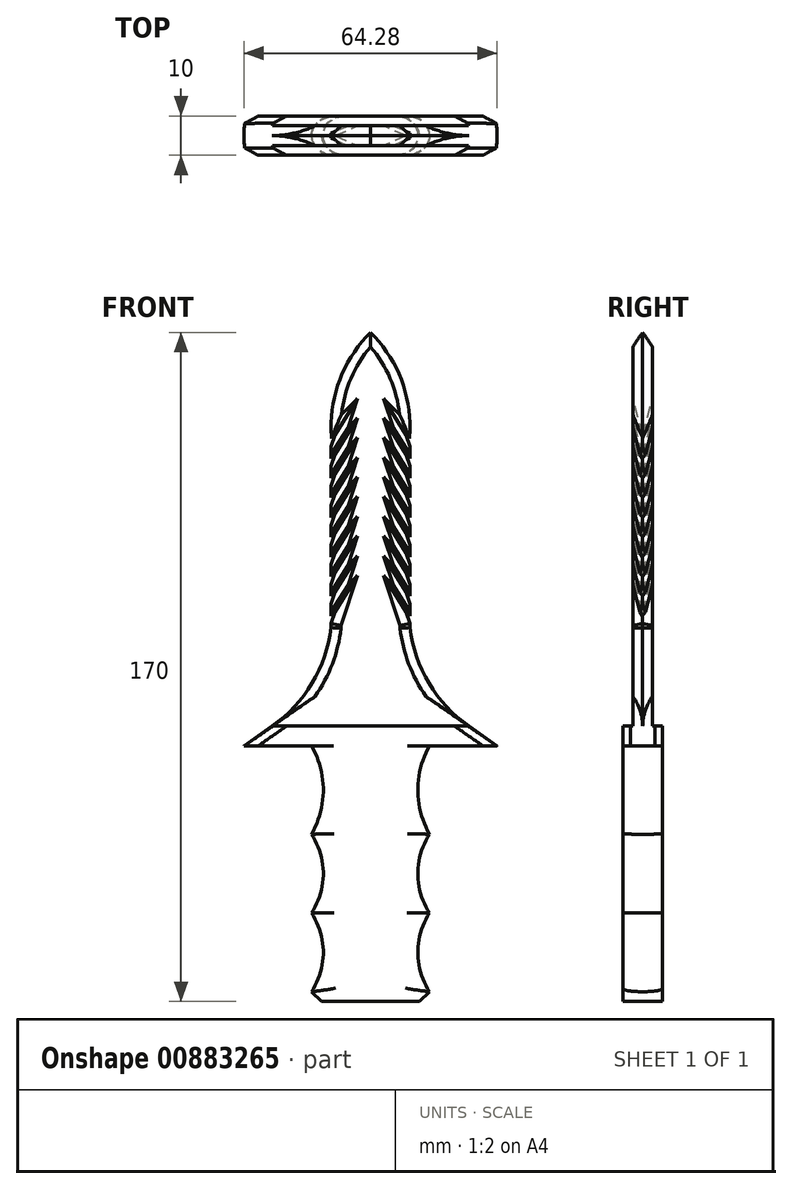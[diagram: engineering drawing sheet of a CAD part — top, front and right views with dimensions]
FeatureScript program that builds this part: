
annotation { "Feature Type Name" : "Feature", "Feature Type Description" : "" }
export const myFeature = defineFeature(function(context is Context, id is Id, definition is map)
    precondition{}
    {
        {
            var Q0;
            Q0=qCreatedBy(makeId("Front.planeOp"),FACE);
            var sketch = newSketch(context, id + "F0", { "sketchPlane" : qUnion([Q0])});
            skLineSegment(sketch, "E0", {"start": v(0, 0) * mm, "end": v(-25, 0) * mm});
            skLineSegment(sketch, "E1", {"start": v(-25, 0) * mm, "end": v(-32.14, -5) * mm});
            skLineSegment(sketch, "E2", {"start": v(-32.14, -5) * mm, "end": v(0, -5) * mm});
            skLineSegment(sketch, "E3", {"start": v(0, 0) * mm, "end": v(0, -5) * mm});
            skLineSegment(sketch, "E4", {"start": v(0, 15.57) * mm, "end": v(0, -20.87) * mm, "construction": true});
            skLineSegment(sketch, "E5", {"start": v(0, -5) * mm, "end": v(0, -70) * mm});
            skLineSegment(sketch, "E6", {"start": v(0, -70) * mm, "end": v(-15, -70) * mm});
            skLineSegment(sketch, "E7", {"start": v(-15, -70) * mm, "end": v(-15, -5) * mm});
            skLineSegment(sketch, "E8", {"start": v(-15, -67.5) * mm, "end": v(-12.5, -70) * mm});
            skLineSegment(sketch, "E9", {"start": v(-10, 25) * mm, "end": v(-10, 77.06) * mm});
            skArc(sketch, "E10", {"start": v(-25, 0) * mm, "mid": v(-14.84, 10.9) * mm, "end": v(-10, 25) * mm});
            skArc(sketch, "E11", {"start": v(0, 100) * mm, "mid": v(-7.6, 88.54) * mm, "end": v(-10, 75) * mm});
            skLineSegment(sketch, "E12", {"start": v(0, 100) * mm, "end": v(0, 0) * mm});
            skArc(sketch, "E13", {"start": v(-15, -67.5) * mm, "mid": v(-12, -57.5) * mm, "end": v(-15, -47.5) * mm});
            skArc(sketch, "E14", {"start": v(-15, -47.5) * mm, "mid": v(-12, -37.5) * mm, "end": v(-15, -27.5) * mm});
            skArc(sketch, "E15", {"start": v(-15, -27.5) * mm, "mid": v(-12, -16.25) * mm, "end": v(-15, -5) * mm});
            skLineSegment(sketch, "E16", {"start": v(-10, 73) * mm, "end": v(-9, 74) * mm});
            skLineSegment(sketch, "E17", {"start": v(-9, 74) * mm, "end": v(-10, 71) * mm});
            skLineSegment(sketch, "E18.1.0.0", {"start": v(-10, 68) * mm, "end": v(-9, 69) * mm});
            skLineSegment(sketch, "E18.1.0.1", {"start": v(-9, 69) * mm, "end": v(-10, 66) * mm});
            skLineSegment(sketch, "E18.2.0.0", {"start": v(-10, 63) * mm, "end": v(-9, 64) * mm});
            skLineSegment(sketch, "E18.2.0.1", {"start": v(-9, 64) * mm, "end": v(-10, 61) * mm});
            skLineSegment(sketch, "E18.3.0.0", {"start": v(-10, 58) * mm, "end": v(-9, 59) * mm});
            skLineSegment(sketch, "E18.3.0.1", {"start": v(-9, 59) * mm, "end": v(-10, 56) * mm});
            skLineSegment(sketch, "E18.4.0.0", {"start": v(-10, 53) * mm, "end": v(-9, 54) * mm});
            skLineSegment(sketch, "E18.4.0.1", {"start": v(-9, 54) * mm, "end": v(-10, 51) * mm});
            skLineSegment(sketch, "E18.5.0.0", {"start": v(-10, 48) * mm, "end": v(-9, 49) * mm});
            skLineSegment(sketch, "E18.5.0.1", {"start": v(-9, 49) * mm, "end": v(-10, 46) * mm});
            skLineSegment(sketch, "E18.6.0.0", {"start": v(-10, 43) * mm, "end": v(-9, 44) * mm});
            skLineSegment(sketch, "E18.6.0.1", {"start": v(-9, 44) * mm, "end": v(-10, 41) * mm});
            skLineSegment(sketch, "E18.7.0.0", {"start": v(-10, 38) * mm, "end": v(-9, 39) * mm});
            skLineSegment(sketch, "E18.7.0.1", {"start": v(-9, 39) * mm, "end": v(-10, 36) * mm});
            skLineSegment(sketch, "E18.8.0.0", {"start": v(-10, 33) * mm, "end": v(-9, 34) * mm});
            skLineSegment(sketch, "E18.8.0.1", {"start": v(-9, 34) * mm, "end": v(-10, 31) * mm});
            skLineSegment(sketch, "E18.9.0.0", {"start": v(-10, 28) * mm, "end": v(-9, 29) * mm});
            skLineSegment(sketch, "E18.9.0.1", {"start": v(-9, 29) * mm, "end": v(-10, 26) * mm});
            skLineSegment(sketch, "E18.direction1", {"start": v(-10, 73) * mm, "end": v(-10, 68) * mm, "construction": true});
            skSolve(sketch);
        }
        {
            var Q0;
            Q0=makeQuery(id+"F0.imprint","IMPRINT",FACE,{"disambiguationData":[TD([[makeQuery(id+"F0.imprint","IMPRINT",EDGE,{"derivedFrom":sQuery(id+"F0.wireOp",EDGE,"E0")}),1.0]])]});
            var Q1;
            {var subQ5=sQuery(id+"F0.wireOp",EDGE,"E5");Q1=makeQuery(id+"F0.imprint","IMPRINT",FACE,{"disambiguationData":[TD([[makeQuery(id+"F0.imprint","IMPRINT",EDGE,{"derivedFrom":subQ5}),-1.0]])]});}
            var Q2;
            Q2=sQuery(id+"F0.wireOp",EDGE,"E4");
            revolve(context, id + "F1", {"surfaceOperationType" : NewSurfaceOperationType.NEW, "entities" : qUnion([Q0, Q1]), "axis" : qUnion([Q2]), "revolveType" : RevolveType.FULL});
        }
        {
            var Q0;
            Q0=makeQuery(id+"F0.imprint","IMPRINT",FACE,{"disambiguationData":[TD([[makeQuery(id+"F0.imprint","IMPRINT",EDGE,{"derivedFrom":sQuery(id+"F0.wireOp",EDGE,"E0")}),-1.0]])]});
            extrude(context, id + "F2", {"entities" : qUnion([Q0]), "operationType" : NewBodyOperationType.ADD, "depth" : 2.5 * mm, "offsetDistance" : 25 * mm});
        }
        {
            var Q0;
            Q0=makeQuery(id+"F2.opExtrude","CAP_EDGE",EDGE,{"disambiguationData":[OSD([sQuery(id+"F0.wireOp",EDGE,"E10")])],"isStart":false});
            var Q1;
            {var subQ0=sQuery(id+"F0.wireOp",EDGE,"E9");Q1=makeQuery(id+"F2.opExtrude","CAP_EDGE",EDGE,{"disambiguationData":[OSD([subQ0]),TDD([makeQuery(id+"F0.imprint","IMPRINT",EDGE,{"disambiguationData":[TD([[makeQuery(id+"F0.imprint","INTERSECT",VERTEX,{"derivedFrom":[subQ0,sQuery(id+"F0.wireOp",EDGE,"E10")]}),-1.0]])],"derivedFrom":subQ0})])],"isStart":false});}
            var Q2;
            Q2=makeQuery(id+"F2.opExtrude","CAP_EDGE",EDGE,{"disambiguationData":[OSD([sQuery(id+"F0.wireOp",EDGE,"E18.9.0.1")])],"isStart":false});
            var Q3;
            Q3=makeQuery(id+"F2.opExtrude","CAP_EDGE",EDGE,{"disambiguationData":[OSD([sQuery(id+"F0.wireOp",EDGE,"E18.9.0.0")])],"isStart":false});
            var Q4;
            {var subQ0=sQuery(id+"F0.wireOp",EDGE,"E9");Q4=makeQuery(id+"F2.opExtrude","CAP_EDGE",EDGE,{"disambiguationData":[OSD([subQ0]),TDD([makeQuery(id+"F0.imprint","IMPRINT",EDGE,{"disambiguationData":[TD([[makeQuery(id+"F0.imprint","INTERSECT",VERTEX,{"derivedFrom":[subQ0,sQuery(id+"F0.wireOp",EDGE,"E18.8.0.1")]}),1.0]])],"derivedFrom":subQ0})])],"isStart":false});}
            var Q5;
            Q5=makeQuery(id+"F2.opExtrude","CAP_EDGE",EDGE,{"disambiguationData":[OSD([sQuery(id+"F0.wireOp",EDGE,"E18.8.0.1")])],"isStart":false});
            var Q6;
            Q6=makeQuery(id+"F2.opExtrude","CAP_EDGE",EDGE,{"disambiguationData":[OSD([sQuery(id+"F0.wireOp",EDGE,"E18.8.0.0")])],"isStart":false});
            var Q7;
            {var subQ0=sQuery(id+"F0.wireOp",EDGE,"E9");Q7=makeQuery(id+"F2.opExtrude","CAP_EDGE",EDGE,{"disambiguationData":[OSD([subQ0]),TDD([makeQuery(id+"F0.imprint","IMPRINT",EDGE,{"disambiguationData":[TD([[makeQuery(id+"F0.imprint","INTERSECT",VERTEX,{"derivedFrom":[subQ0,sQuery(id+"F0.wireOp",EDGE,"E18.7.0.1")]}),1.0]])],"derivedFrom":subQ0})])],"isStart":false});}
            var Q8;
            Q8=makeQuery(id+"F2.opExtrude","CAP_EDGE",EDGE,{"disambiguationData":[OSD([sQuery(id+"F0.wireOp",EDGE,"E18.7.0.1")])],"isStart":false});
            var Q9;
            Q9=makeQuery(id+"F2.opExtrude","CAP_EDGE",EDGE,{"disambiguationData":[OSD([sQuery(id+"F0.wireOp",EDGE,"E18.7.0.0")])],"isStart":false});
            var Q10;
            {var subQ0=sQuery(id+"F0.wireOp",EDGE,"E9");Q10=makeQuery(id+"F2.opExtrude","CAP_EDGE",EDGE,{"disambiguationData":[OSD([subQ0]),TDD([makeQuery(id+"F0.imprint","IMPRINT",EDGE,{"disambiguationData":[TD([[makeQuery(id+"F0.imprint","INTERSECT",VERTEX,{"derivedFrom":[subQ0,sQuery(id+"F0.wireOp",EDGE,"E18.6.0.1")]}),1.0]])],"derivedFrom":subQ0})])],"isStart":false});}
            var Q11;
            Q11=makeQuery(id+"F2.opExtrude","CAP_EDGE",EDGE,{"disambiguationData":[OSD([sQuery(id+"F0.wireOp",EDGE,"E18.6.0.1")])],"isStart":false});
            var Q12;
            Q12=makeQuery(id+"F2.opExtrude","CAP_EDGE",EDGE,{"disambiguationData":[OSD([sQuery(id+"F0.wireOp",EDGE,"E18.6.0.0")])],"isStart":false});
            var Q13;
            {var subQ0=sQuery(id+"F0.wireOp",EDGE,"E9");Q13=makeQuery(id+"F2.opExtrude","CAP_EDGE",EDGE,{"disambiguationData":[OSD([subQ0]),TDD([makeQuery(id+"F0.imprint","IMPRINT",EDGE,{"disambiguationData":[TD([[makeQuery(id+"F0.imprint","INTERSECT",VERTEX,{"derivedFrom":[subQ0,sQuery(id+"F0.wireOp",EDGE,"E18.5.0.1")]}),1.0]])],"derivedFrom":subQ0})])],"isStart":false});}
            var Q14;
            Q14=makeQuery(id+"F2.opExtrude","CAP_EDGE",EDGE,{"disambiguationData":[OSD([sQuery(id+"F0.wireOp",EDGE,"E18.5.0.1")])],"isStart":false});
            var Q15;
            Q15=makeQuery(id+"F2.opExtrude","CAP_EDGE",EDGE,{"disambiguationData":[OSD([sQuery(id+"F0.wireOp",EDGE,"E18.5.0.0")])],"isStart":false});
            var Q16;
            {var subQ0=sQuery(id+"F0.wireOp",EDGE,"E9");Q16=makeQuery(id+"F2.opExtrude","CAP_EDGE",EDGE,{"disambiguationData":[OSD([subQ0]),TDD([makeQuery(id+"F0.imprint","IMPRINT",EDGE,{"disambiguationData":[TD([[makeQuery(id+"F0.imprint","INTERSECT",VERTEX,{"derivedFrom":[subQ0,sQuery(id+"F0.wireOp",EDGE,"E18.4.0.1")]}),1.0]])],"derivedFrom":subQ0})])],"isStart":false});}
            var Q17;
            Q17=makeQuery(id+"F2.opExtrude","CAP_EDGE",EDGE,{"disambiguationData":[OSD([sQuery(id+"F0.wireOp",EDGE,"E18.4.0.1")])],"isStart":false});
            var Q18;
            Q18=makeQuery(id+"F2.opExtrude","CAP_EDGE",EDGE,{"disambiguationData":[OSD([sQuery(id+"F0.wireOp",EDGE,"E18.4.0.0")])],"isStart":false});
            var Q19;
            {var subQ0=sQuery(id+"F0.wireOp",EDGE,"E9");Q19=makeQuery(id+"F2.opExtrude","CAP_EDGE",EDGE,{"disambiguationData":[OSD([subQ0]),TDD([makeQuery(id+"F0.imprint","IMPRINT",EDGE,{"disambiguationData":[TD([[makeQuery(id+"F0.imprint","INTERSECT",VERTEX,{"derivedFrom":[subQ0,sQuery(id+"F0.wireOp",EDGE,"E18.3.0.1")]}),1.0]])],"derivedFrom":subQ0})])],"isStart":false});}
            var Q20;
            Q20=makeQuery(id+"F2.opExtrude","CAP_EDGE",EDGE,{"disambiguationData":[OSD([sQuery(id+"F0.wireOp",EDGE,"E18.3.0.1")])],"isStart":false});
            var Q21;
            Q21=makeQuery(id+"F2.opExtrude","CAP_EDGE",EDGE,{"disambiguationData":[OSD([sQuery(id+"F0.wireOp",EDGE,"E18.3.0.0")])],"isStart":false});
            var Q22;
            {var subQ0=sQuery(id+"F0.wireOp",EDGE,"E9");Q22=makeQuery(id+"F2.opExtrude","CAP_EDGE",EDGE,{"disambiguationData":[OSD([subQ0]),TDD([makeQuery(id+"F0.imprint","IMPRINT",EDGE,{"disambiguationData":[TD([[makeQuery(id+"F0.imprint","INTERSECT",VERTEX,{"derivedFrom":[subQ0,sQuery(id+"F0.wireOp",EDGE,"E18.2.0.1")]}),1.0]])],"derivedFrom":subQ0})])],"isStart":false});}
            var Q23;
            Q23=makeQuery(id+"F2.opExtrude","CAP_EDGE",EDGE,{"disambiguationData":[OSD([sQuery(id+"F0.wireOp",EDGE,"E18.2.0.1")])],"isStart":false});
            var Q24;
            Q24=makeQuery(id+"F2.opExtrude","CAP_EDGE",EDGE,{"disambiguationData":[OSD([sQuery(id+"F0.wireOp",EDGE,"E18.2.0.0")])],"isStart":false});
            var Q25;
            {var subQ0=sQuery(id+"F0.wireOp",EDGE,"E9");Q25=makeQuery(id+"F2.opExtrude","CAP_EDGE",EDGE,{"disambiguationData":[OSD([subQ0]),TDD([makeQuery(id+"F0.imprint","IMPRINT",EDGE,{"disambiguationData":[TD([[makeQuery(id+"F0.imprint","INTERSECT",VERTEX,{"derivedFrom":[subQ0,sQuery(id+"F0.wireOp",EDGE,"E18.1.0.1")]}),1.0]])],"derivedFrom":subQ0})])],"isStart":false});}
            var Q26;
            Q26=makeQuery(id+"F2.opExtrude","CAP_EDGE",EDGE,{"disambiguationData":[OSD([sQuery(id+"F0.wireOp",EDGE,"E18.1.0.1")])],"isStart":false});
            var Q27;
            Q27=makeQuery(id+"F2.opExtrude","CAP_EDGE",EDGE,{"disambiguationData":[OSD([sQuery(id+"F0.wireOp",EDGE,"E18.1.0.0")])],"isStart":false});
            var Q28;
            {var subQ0=sQuery(id+"F0.wireOp",EDGE,"E9");Q28=makeQuery(id+"F2.opExtrude","CAP_EDGE",EDGE,{"disambiguationData":[OSD([subQ0]),TDD([makeQuery(id+"F0.imprint","IMPRINT",EDGE,{"disambiguationData":[TD([[makeQuery(id+"F0.imprint","INTERSECT",VERTEX,{"derivedFrom":[subQ0,sQuery(id+"F0.wireOp",EDGE,"E17")]}),1.0]])],"derivedFrom":subQ0})])],"isStart":false});}
            var Q29;
            Q29=makeQuery(id+"F2.opExtrude","CAP_EDGE",EDGE,{"disambiguationData":[OSD([sQuery(id+"F0.wireOp",EDGE,"E17")])],"isStart":false});
            var Q30;
            Q30=makeQuery(id+"F2.opExtrude","CAP_EDGE",EDGE,{"disambiguationData":[OSD([sQuery(id+"F0.wireOp",EDGE,"E16")])],"isStart":false});
            var Q31;
            {var subQ0=sQuery(id+"F0.wireOp",EDGE,"E11");var subQ1=sQuery(id+"F0.wireOp",EDGE,"E9");var subQ2=makeQuery(id+"F0.imprint","INTERSECT",VERTEX,{"disambiguationData":[OD(1.0)],"derivedFrom":[subQ1,subQ0]});Q31=makeQuery(id+"F2.opExtrude","CAP_EDGE",EDGE,{"disambiguationData":[OSD([subQ1]),TDD([makeQuery(id+"F0.imprint","IMPRINT",EDGE,{"disambiguationData":[TD([[subQ2,1.0]])],"derivedFrom":subQ1}),makeQuery(id+"F0.imprint","IMPRINT",EDGE,{"disambiguationData":[TD([[makeQuery(id+"F0.imprint","INTERSECT",VERTEX,{"disambiguationData":[OD(0.0)],"derivedFrom":[subQ1,subQ0]}),1.0]])],"derivedFrom":subQ1})])],"isStart":false});}
            var Q32;
            Q32=makeQuery(id+"F2.opExtrude","CAP_EDGE",EDGE,{"disambiguationData":[OSD([sQuery(id+"F0.wireOp",EDGE,"E11")])],"isStart":false});
            chamfer(context, id + "F3", {"entities" : qUnion([Q0, Q1, Q2, Q3, Q4, Q5, Q6, Q7, Q8, Q9, Q10, Q11, Q12, Q13, Q14, Q15, Q16, Q17, Q18, Q19, Q20, Q21, Q22, Q23, Q24, Q25, Q26, Q27, Q28, Q29, Q30, Q31, Q32]), "width" : 2.5 * mm, "tangentPropagation" : true});
        }
        {
            var Q0;
            Q0=makeQuery(id+"F1.opRevolve","SWEPT_BODY",BODY,{"disambiguationData":[OSD([sQuery(id+"F0.wireOp",EDGE,"E0"),sQuery(id+"F0.wireOp",EDGE,"E1"),sQuery(id+"F0.wireOp",EDGE,"E2"),sQuery(id+"F0.wireOp",EDGE,"E3"),sQuery(id+"F0.wireOp",EDGE,"E5"),sQuery(id+"F0.wireOp",EDGE,"E6"),sQuery(id+"F0.wireOp",EDGE,"E8"),sQuery(id+"F0.wireOp",EDGE,"E13"),sQuery(id+"F0.wireOp",EDGE,"E14"),sQuery(id+"F0.wireOp",EDGE,"E15")])]});
            var Q1;
            Q1=makeQuery(id+"F0.imprint","IMPRINT",FACE,{"disambiguationData":[TD([[makeQuery(id+"F0.imprint","IMPRINT",EDGE,{"derivedFrom":sQuery(id+"F0.wireOp",EDGE,"E0")}),-1.0]])]});
            mirror(context, id + "F4", {"operationType" : NewBodyOperationType.ADD, "entities" : qUnion([Q0]), "mirrorPlane" : qUnion([Q1])});
        }
        {
            var Q0;
            Q0=makeQuery(id+"F1.opRevolve","SWEPT_BODY",BODY,{"disambiguationData":[OSD([sQuery(id+"F0.wireOp",EDGE,"E0"),sQuery(id+"F0.wireOp",EDGE,"E1"),sQuery(id+"F0.wireOp",EDGE,"E2"),sQuery(id+"F0.wireOp",EDGE,"E3"),sQuery(id+"F0.wireOp",EDGE,"E5"),sQuery(id+"F0.wireOp",EDGE,"E6"),sQuery(id+"F0.wireOp",EDGE,"E8"),sQuery(id+"F0.wireOp",EDGE,"E13"),sQuery(id+"F0.wireOp",EDGE,"E14"),sQuery(id+"F0.wireOp",EDGE,"E15")])]});
            var Q1;
            {var subQ0=makeQuery(id+"F2.opExtrude","SWEPT_FACE",FACE,{"disambiguationData":[OSD([sQuery(id+"F0.wireOp",EDGE,"E12")])]});Q1=makeQuery(id+"F4.boolean.opBoolean","MERGE",FACE,{"derivedFrom":[subQ0,makeQuery(id+"F4.opPattern","COPY",FACE,{"derivedFrom":subQ0,"instanceName":"1"})]});}
            mirror(context, id + "F5", {"operationType" : NewBodyOperationType.ADD, "entities" : qUnion([Q0]), "mirrorPlane" : qUnion([Q1])});
        }
        {
            var Q0;
            Q0=makeQuery(id+"F1.opRevolve","SWEPT_FACE",FACE,{"disambiguationData":[OSD([sQuery(id+"F0.wireOp",EDGE,"E6")])]});
            var sketch = newSketch(context, id + "F6", { "sketchPlane" : qUnion([Q0])});
            skLineSegment(sketch, "E19.bottom", {"start": v(-35, 5) * mm, "end": v(35, 5) * mm});
            skLineSegment(sketch, "E19.top", {"start": v(-35, 40) * mm, "end": v(35, 40) * mm});
            skLineSegment(sketch, "E19.left", {"start": v(-35, 5) * mm, "end": v(-35, 40) * mm});
            skLineSegment(sketch, "E19.right", {"start": v(35, 5) * mm, "end": v(35, 40) * mm});
            skPoint(sketch, "E19.middle", {"position": v(0, 22.5) * mm});
            skLineSegment(sketch, "E20.bottom", {"start": v(-35, -5) * mm, "end": v(35, -5) * mm});
            skLineSegment(sketch, "E20.top", {"start": v(-35, -40) * mm, "end": v(35, -40) * mm});
            skLineSegment(sketch, "E20.left", {"start": v(-35, -5) * mm, "end": v(-35, -40) * mm});
            skLineSegment(sketch, "E20.right", {"start": v(35, -5) * mm, "end": v(35, -40) * mm});
            skPoint(sketch, "E20.middle", {"position": v(0, -22.5) * mm});
            skSolve(sketch);
        }
        {
            var Q0;
            Q0=makeQuery(id+"F6.imprint","IMPRINT",FACE,{"disambiguationData":[TD([[makeQuery(id+"F6.imprint","IMPRINT",EDGE,{"derivedFrom":sQuery(id+"F6.wireOp",EDGE,"E19.top")}),-1.0]])]});
            var Q1;
            Q1=makeQuery(id+"F6.imprint","IMPRINT",FACE,{"disambiguationData":[TD([[makeQuery(id+"F6.imprint","IMPRINT",EDGE,{"derivedFrom":sQuery(id+"F6.wireOp",EDGE,"E20.top")}),1.0]])]});
            var Q2;
            {var subQ0=sQuery(id+"F6.wireOp",EDGE,"E20.bottom");var subQ1=makeQuery(id+"F1.opRevolve","SWEPT_EDGE",EDGE,{"disambiguationData":[OSD([sQuery(id+"F0.wireOp",EDGE,"E6"),sQuery(id+"F0.wireOp",EDGE,"E8")])]});var subQ2=makeQuery(id+"F6.imprint","INTERSECT",VERTEX,{"disambiguationData":[OD(0.0)],"derivedFrom":[subQ1,subQ0]});Q2=makeQuery(id+"F6.imprint","IMPRINT",FACE,{"disambiguationData":[TD([[makeQuery(id+"F6.imprint","IMPRINT",EDGE,{"disambiguationData":[TD([[subQ2,-1.0]])],"derivedFrom":subQ0}),-1.0]])]});}
            var Q3;
            {var subQ0=sQuery(id+"F6.wireOp",EDGE,"E19.bottom");var subQ1=makeQuery(id+"F1.opRevolve","SWEPT_EDGE",EDGE,{"disambiguationData":[OSD([sQuery(id+"F0.wireOp",EDGE,"E6"),sQuery(id+"F0.wireOp",EDGE,"E8")])]});var subQ2=makeQuery(id+"F6.imprint","INTERSECT",VERTEX,{"disambiguationData":[OD(0.0)],"derivedFrom":[subQ1,subQ0]});Q3=makeQuery(id+"F6.imprint","IMPRINT",FACE,{"disambiguationData":[TD([[makeQuery(id+"F6.imprint","IMPRINT",EDGE,{"disambiguationData":[TD([[subQ2,-1.0]])],"derivedFrom":subQ0}),1.0]])]});}
            var Q4;
            {var subQ0=sQuery(id+"F0.wireOp",EDGE,"E0");var subQ1=makeQuery(id+"F2.opExtrude","CAP_FACE",FACE,{"disambiguationData":[OSD([subQ0,sQuery(id+"F0.wireOp",EDGE,"E9"),sQuery(id+"F0.wireOp",EDGE,"E10"),sQuery(id+"F0.wireOp",EDGE,"E11"),sQuery(id+"F0.wireOp",EDGE,"E12"),sQuery(id+"F0.wireOp",EDGE,"E16"),sQuery(id+"F0.wireOp",EDGE,"E17"),sQuery(id+"F0.wireOp",EDGE,"E18.1.0.0"),sQuery(id+"F0.wireOp",EDGE,"E18.1.0.1"),sQuery(id+"F0.wireOp",EDGE,"E18.2.0.0"),sQuery(id+"F0.wireOp",EDGE,"E18.2.0.1"),sQuery(id+"F0.wireOp",EDGE,"E18.3.0.0"),sQuery(id+"F0.wireOp",EDGE,"E18.3.0.1"),sQuery(id+"F0.wireOp",EDGE,"E18.4.0.0"),sQuery(id+"F0.wireOp",EDGE,"E18.4.0.1"),sQuery(id+"F0.wireOp",EDGE,"E18.5.0.0"),sQuery(id+"F0.wireOp",EDGE,"E18.5.0.1"),sQuery(id+"F0.wireOp",EDGE,"E18.6.0.0"),sQuery(id+"F0.wireOp",EDGE,"E18.6.0.1"),sQuery(id+"F0.wireOp",EDGE,"E18.7.0.0"),sQuery(id+"F0.wireOp",EDGE,"E18.7.0.1"),sQuery(id+"F0.wireOp",EDGE,"E18.8.0.0"),sQuery(id+"F0.wireOp",EDGE,"E18.8.0.1"),sQuery(id+"F0.wireOp",EDGE,"E18.9.0.0"),sQuery(id+"F0.wireOp",EDGE,"E18.9.0.1")])],"isStart":false});Q4=makeQuery(id+"F5.boolean.opBoolean","SPLIT",FACE,{"disambiguationData":[TD([subQ1])],"derivedFrom":makeQuery(id+"F1.opRevolve","SWEPT_FACE",FACE,{"disambiguationData":[OSD([subQ0])]})});}
            extrude(context, id + "F7", {"entities" : qUnion([Q0, Q1, Q2, Q3]), "operationType" : NewBodyOperationType.REMOVE, "endBound" : BoundingType.UP_TO_SURFACE, "oppositeDirection" : true, "depth" : 25 * mm, "endBoundEntityFace" : qUnion([Q4]), "offsetDistance" : 25 * mm});
        }
        {
            var Q0;
            Q0=makeQuery(id+"F7.boolean.opBoolean","INTERSECT",EDGE,{"disambiguationData":[OD(0.0)],"derivedFrom":[makeQuery(id+"F1.opRevolve","SWEPT_FACE",FACE,{"disambiguationData":[OSD([sQuery(id+"F0.wireOp",EDGE,"E15")])]}),makeQuery(id+"F7.opExtrude","SWEPT_FACE",FACE,{"disambiguationData":[OSD([sQuery(id+"F6.wireOp",EDGE,"E19.bottom")])]})]});
            var Q1;
            Q1=makeQuery(id+"F7.boolean.opBoolean","INTERSECT",EDGE,{"disambiguationData":[OD(0.0)],"derivedFrom":[makeQuery(id+"F1.opRevolve","SWEPT_FACE",FACE,{"disambiguationData":[OSD([sQuery(id+"F0.wireOp",EDGE,"E14")])]}),makeQuery(id+"F7.opExtrude","SWEPT_FACE",FACE,{"disambiguationData":[OSD([sQuery(id+"F6.wireOp",EDGE,"E19.bottom")])]})]});
            var Q2;
            Q2=makeQuery(id+"F7.boolean.opBoolean","INTERSECT",EDGE,{"disambiguationData":[OD(0.0)],"derivedFrom":[makeQuery(id+"F1.opRevolve","SWEPT_FACE",FACE,{"disambiguationData":[OSD([sQuery(id+"F0.wireOp",EDGE,"E13")])]}),makeQuery(id+"F7.opExtrude","SWEPT_FACE",FACE,{"disambiguationData":[OSD([sQuery(id+"F6.wireOp",EDGE,"E19.bottom")])]})]});
            var Q3;
            Q3=makeQuery(id+"F7.boolean.opBoolean","INTERSECT",EDGE,{"disambiguationData":[OD(0.0)],"derivedFrom":[makeQuery(id+"F1.opRevolve","SWEPT_FACE",FACE,{"disambiguationData":[OSD([sQuery(id+"F0.wireOp",EDGE,"E8")])]}),makeQuery(id+"F7.opExtrude","SWEPT_FACE",FACE,{"disambiguationData":[OSD([sQuery(id+"F6.wireOp",EDGE,"E19.bottom")])]})]});
            var Q4;
            Q4=makeQuery(id+"F7.boolean.opBoolean","INTERSECT",EDGE,{"disambiguationData":[OD(1.0)],"derivedFrom":[makeQuery(id+"F1.opRevolve","SWEPT_FACE",FACE,{"disambiguationData":[OSD([sQuery(id+"F0.wireOp",EDGE,"E8")])]}),makeQuery(id+"F7.opExtrude","SWEPT_FACE",FACE,{"disambiguationData":[OSD([sQuery(id+"F6.wireOp",EDGE,"E19.bottom")])]})]});
            var Q5;
            Q5=makeQuery(id+"F7.boolean.opBoolean","INTERSECT",EDGE,{"disambiguationData":[OD(1.0)],"derivedFrom":[makeQuery(id+"F1.opRevolve","SWEPT_FACE",FACE,{"disambiguationData":[OSD([sQuery(id+"F0.wireOp",EDGE,"E13")])]}),makeQuery(id+"F7.opExtrude","SWEPT_FACE",FACE,{"disambiguationData":[OSD([sQuery(id+"F6.wireOp",EDGE,"E19.bottom")])]})]});
            var Q6;
            Q6=makeQuery(id+"F7.boolean.opBoolean","INTERSECT",EDGE,{"disambiguationData":[OD(1.0)],"derivedFrom":[makeQuery(id+"F1.opRevolve","SWEPT_FACE",FACE,{"disambiguationData":[OSD([sQuery(id+"F0.wireOp",EDGE,"E14")])]}),makeQuery(id+"F7.opExtrude","SWEPT_FACE",FACE,{"disambiguationData":[OSD([sQuery(id+"F6.wireOp",EDGE,"E19.bottom")])]})]});
            var Q7;
            Q7=makeQuery(id+"F7.boolean.opBoolean","INTERSECT",EDGE,{"disambiguationData":[OD(1.0)],"derivedFrom":[makeQuery(id+"F1.opRevolve","SWEPT_FACE",FACE,{"disambiguationData":[OSD([sQuery(id+"F0.wireOp",EDGE,"E15")])]}),makeQuery(id+"F7.opExtrude","SWEPT_FACE",FACE,{"disambiguationData":[OSD([sQuery(id+"F6.wireOp",EDGE,"E19.bottom")])]})]});
            var Q8;
            Q8=makeQuery(id+"F7.boolean.opBoolean","INTERSECT",EDGE,{"disambiguationData":[OD(1.0)],"derivedFrom":[makeQuery(id+"F1.opRevolve","SWEPT_FACE",FACE,{"disambiguationData":[OSD([sQuery(id+"F0.wireOp",EDGE,"E15")])]}),makeQuery(id+"F7.opExtrude","SWEPT_FACE",FACE,{"disambiguationData":[OSD([sQuery(id+"F6.wireOp",EDGE,"E20.bottom")])]})]});
            var Q9;
            Q9=makeQuery(id+"F7.boolean.opBoolean","INTERSECT",EDGE,{"disambiguationData":[OD(1.0)],"derivedFrom":[makeQuery(id+"F1.opRevolve","SWEPT_FACE",FACE,{"disambiguationData":[OSD([sQuery(id+"F0.wireOp",EDGE,"E14")])]}),makeQuery(id+"F7.opExtrude","SWEPT_FACE",FACE,{"disambiguationData":[OSD([sQuery(id+"F6.wireOp",EDGE,"E20.bottom")])]})]});
            var Q10;
            Q10=makeQuery(id+"F7.boolean.opBoolean","INTERSECT",EDGE,{"disambiguationData":[OD(1.0)],"derivedFrom":[makeQuery(id+"F1.opRevolve","SWEPT_FACE",FACE,{"disambiguationData":[OSD([sQuery(id+"F0.wireOp",EDGE,"E13")])]}),makeQuery(id+"F7.opExtrude","SWEPT_FACE",FACE,{"disambiguationData":[OSD([sQuery(id+"F6.wireOp",EDGE,"E20.bottom")])]})]});
            var Q11;
            Q11=makeQuery(id+"F7.boolean.opBoolean","INTERSECT",EDGE,{"disambiguationData":[OD(1.0)],"derivedFrom":[makeQuery(id+"F1.opRevolve","SWEPT_FACE",FACE,{"disambiguationData":[OSD([sQuery(id+"F0.wireOp",EDGE,"E8")])]}),makeQuery(id+"F7.opExtrude","SWEPT_FACE",FACE,{"disambiguationData":[OSD([sQuery(id+"F6.wireOp",EDGE,"E20.bottom")])]})]});
            var Q12;
            Q12=makeQuery(id+"F7.boolean.opBoolean","INTERSECT",EDGE,{"disambiguationData":[OD(0.0)],"derivedFrom":[makeQuery(id+"F1.opRevolve","SWEPT_FACE",FACE,{"disambiguationData":[OSD([sQuery(id+"F0.wireOp",EDGE,"E8")])]}),makeQuery(id+"F7.opExtrude","SWEPT_FACE",FACE,{"disambiguationData":[OSD([sQuery(id+"F6.wireOp",EDGE,"E20.bottom")])]})]});
            var Q13;
            Q13=makeQuery(id+"F7.boolean.opBoolean","INTERSECT",EDGE,{"disambiguationData":[OD(0.0)],"derivedFrom":[makeQuery(id+"F1.opRevolve","SWEPT_FACE",FACE,{"disambiguationData":[OSD([sQuery(id+"F0.wireOp",EDGE,"E13")])]}),makeQuery(id+"F7.opExtrude","SWEPT_FACE",FACE,{"disambiguationData":[OSD([sQuery(id+"F6.wireOp",EDGE,"E20.bottom")])]})]});
            var Q14;
            Q14=makeQuery(id+"F7.boolean.opBoolean","INTERSECT",EDGE,{"disambiguationData":[OD(0.0)],"derivedFrom":[makeQuery(id+"F1.opRevolve","SWEPT_FACE",FACE,{"disambiguationData":[OSD([sQuery(id+"F0.wireOp",EDGE,"E14")])]}),makeQuery(id+"F7.opExtrude","SWEPT_FACE",FACE,{"disambiguationData":[OSD([sQuery(id+"F6.wireOp",EDGE,"E20.bottom")])]})]});
            var Q15;
            Q15=makeQuery(id+"F7.boolean.opBoolean","INTERSECT",EDGE,{"disambiguationData":[OD(0.0)],"derivedFrom":[makeQuery(id+"F1.opRevolve","SWEPT_FACE",FACE,{"disambiguationData":[OSD([sQuery(id+"F0.wireOp",EDGE,"E15")])]}),makeQuery(id+"F7.opExtrude","SWEPT_FACE",FACE,{"disambiguationData":[OSD([sQuery(id+"F6.wireOp",EDGE,"E20.bottom")])]})]});
            fillet(context, id + "F8", {"entities" : qUnion([Q0, Q1, Q2, Q3, Q4, Q5, Q6, Q7, Q8, Q9, Q10, Q11, Q12, Q13, Q14, Q15]), "radius" : 5 * mm, "tangentPropagation" : true, "allowEdgeOverflow" : false});
        }
        {
            var Q0;
            {var subQ0=makeQuery(id+"F1.opRevolve","SWEPT_FACE",FACE,{"disambiguationData":[OSD([sQuery(id+"F0.wireOp",EDGE,"E1")])]});var subQ1=makeQuery(id+"F4.boolean.opBoolean","MERGE",FACE,{"derivedFrom":[subQ0,makeQuery(id+"F4.opPattern","COPY",FACE,{"derivedFrom":subQ0,"instanceName":"1"})]});Q0=makeQuery(id+"F7.boolean.opBoolean","INTERSECT",EDGE,{"disambiguationData":[OD(1.0)],"derivedFrom":[makeQuery(id+"F5.boolean.opBoolean","MERGE",FACE,{"derivedFrom":[subQ1,makeQuery(id+"F5.opPattern","COPY",FACE,{"derivedFrom":subQ1,"instanceName":"1"})]}),makeQuery(id+"F7.opExtrude","SWEPT_FACE",FACE,{"disambiguationData":[OSD([sQuery(id+"F6.wireOp",EDGE,"E20.bottom")])]})]});}
            var Q1;
            {var subQ0=makeQuery(id+"F1.opRevolve","SWEPT_FACE",FACE,{"disambiguationData":[OSD([sQuery(id+"F0.wireOp",EDGE,"E1")])]});var subQ1=makeQuery(id+"F4.boolean.opBoolean","MERGE",FACE,{"derivedFrom":[subQ0,makeQuery(id+"F4.opPattern","COPY",FACE,{"derivedFrom":subQ0,"instanceName":"1"})]});Q1=makeQuery(id+"F7.boolean.opBoolean","INTERSECT",EDGE,{"disambiguationData":[OD(0.0)],"derivedFrom":[makeQuery(id+"F5.boolean.opBoolean","MERGE",FACE,{"derivedFrom":[subQ1,makeQuery(id+"F5.opPattern","COPY",FACE,{"derivedFrom":subQ1,"instanceName":"1"})]}),makeQuery(id+"F7.opExtrude","SWEPT_FACE",FACE,{"disambiguationData":[OSD([sQuery(id+"F6.wireOp",EDGE,"E20.bottom")])]})]});}
            var Q2;
            {var subQ0=makeQuery(id+"F1.opRevolve","SWEPT_FACE",FACE,{"disambiguationData":[OSD([sQuery(id+"F0.wireOp",EDGE,"E1")])]});var subQ1=makeQuery(id+"F4.boolean.opBoolean","MERGE",FACE,{"derivedFrom":[subQ0,makeQuery(id+"F4.opPattern","COPY",FACE,{"derivedFrom":subQ0,"instanceName":"1"})]});Q2=makeQuery(id+"F7.boolean.opBoolean","INTERSECT",EDGE,{"disambiguationData":[OD(1.0)],"derivedFrom":[makeQuery(id+"F5.boolean.opBoolean","MERGE",FACE,{"derivedFrom":[subQ1,makeQuery(id+"F5.opPattern","COPY",FACE,{"derivedFrom":subQ1,"instanceName":"1"})]}),makeQuery(id+"F7.opExtrude","SWEPT_FACE",FACE,{"disambiguationData":[OSD([sQuery(id+"F6.wireOp",EDGE,"E19.bottom")])]})]});}
            var Q3;
            {var subQ0=makeQuery(id+"F1.opRevolve","SWEPT_FACE",FACE,{"disambiguationData":[OSD([sQuery(id+"F0.wireOp",EDGE,"E1")])]});var subQ1=makeQuery(id+"F4.boolean.opBoolean","MERGE",FACE,{"derivedFrom":[subQ0,makeQuery(id+"F4.opPattern","COPY",FACE,{"derivedFrom":subQ0,"instanceName":"1"})]});Q3=makeQuery(id+"F7.boolean.opBoolean","INTERSECT",EDGE,{"disambiguationData":[OD(0.0)],"derivedFrom":[makeQuery(id+"F5.boolean.opBoolean","MERGE",FACE,{"derivedFrom":[subQ1,makeQuery(id+"F5.opPattern","COPY",FACE,{"derivedFrom":subQ1,"instanceName":"1"})]}),makeQuery(id+"F7.opExtrude","SWEPT_FACE",FACE,{"disambiguationData":[OSD([sQuery(id+"F6.wireOp",EDGE,"E19.bottom")])]})]});}
            chamfer(context, id + "F9", {"entities" : qUnion([Q0, Q1, Q2, Q3]), "width" : 2 * mm, "tangentPropagation" : true});
        }
    });
